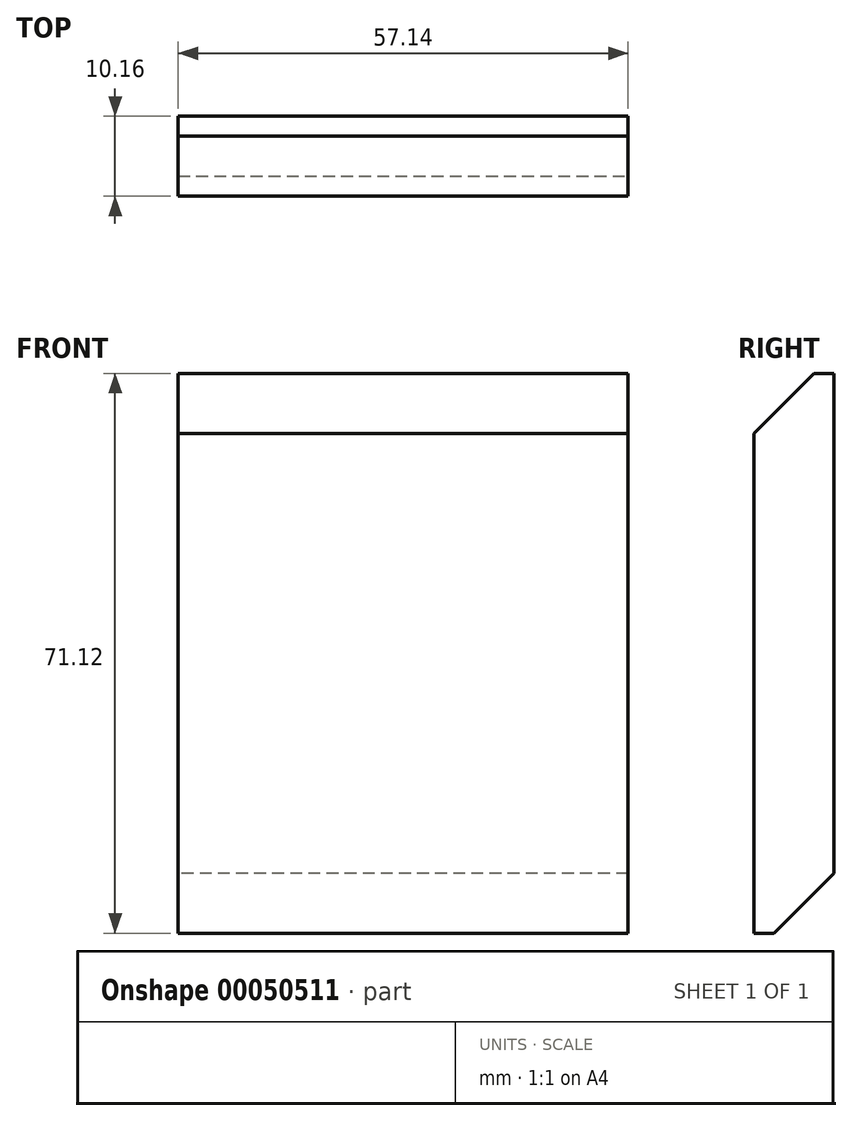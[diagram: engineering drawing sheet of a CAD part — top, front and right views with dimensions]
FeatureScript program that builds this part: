
annotation { "Feature Type Name" : "Feature", "Feature Type Description" : "" }
export const myFeature = defineFeature(function(context is Context, id is Id, definition is map)
    precondition{}
    {
        {
            var Q0;
            Q0=qCreatedBy(makeId("Front.planeOp"),FACE);
            var sketch = newSketch(context, id + "F0", { "sketchPlane" : qUnion([Q0])});
            skLineSegment(sketch, "E0.rect.bottom", {"start": v(28.58, 35.56) * mm, "end": v(-28.58, 35.56) * mm});
            skLineSegment(sketch, "E0.rect.top", {"start": v(28.58, -35.56) * mm, "end": v(-28.58, -35.56) * mm});
            skLineSegment(sketch, "E0.rect.left", {"start": v(28.58, 35.56) * mm, "end": v(28.58, -35.56) * mm});
            skLineSegment(sketch, "E0.rect.right", {"start": v(-28.58, 35.56) * mm, "end": v(-28.58, -35.56) * mm});
            skPoint(sketch, "E0.rect.middle", {"position": v(0, 0) * mm});
            skSolve(sketch);
        }
        {
            var Q0;
            Q0=qSketchRegion(id+"F0",true);
            extrude(context, id + "F1", {"entities" : qUnion([Q0]), "endBound" : BoundingType.SYMMETRIC, "depth" : 10.16 * mm});
        }
        {
            var Q0;
            Q0=makeQuery(id+"F1.opExtrude","CAP_EDGE",EDGE,{"disambiguationData":[OSD([sQuery(id+"F0.wireOp",EDGE,"E0.rect.bottom")])],"isStart":false});
            var Q1;
            Q1=makeQuery(id+"F1.opExtrude","CAP_EDGE",EDGE,{"disambiguationData":[OSD([sQuery(id+"F0.wireOp",EDGE,"E0.rect.top")])],"isStart":true});
            chamfer(context, id + "F2", {"entities" : qUnion([Q0, Q1]), "width" : 7.62 * mm, "tangentPropagation" : true});
        }
    });
